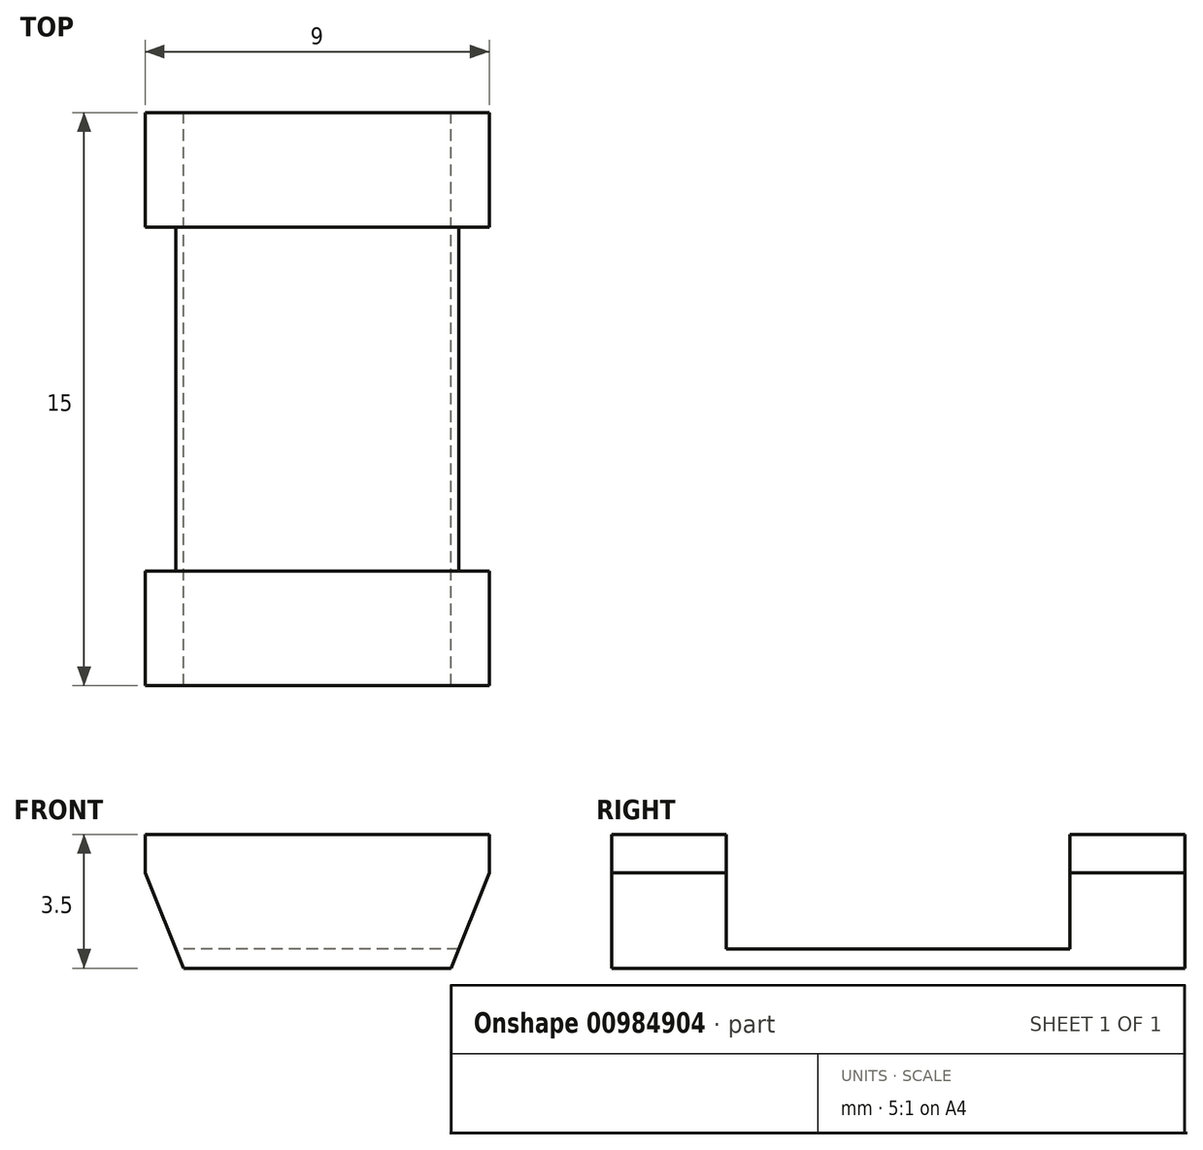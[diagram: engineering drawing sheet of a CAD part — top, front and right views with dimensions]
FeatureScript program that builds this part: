
annotation { "Feature Type Name" : "Feature", "Feature Type Description" : "" }
export const myFeature = defineFeature(function(context is Context, id is Id, definition is map)
    precondition{}
    {
        {
            var Q0;
            Q0=qCreatedBy(makeId("Front.planeOp"),FACE);
            var sketch = newSketch(context, id + "F0", { "sketchPlane" : qUnion([Q0])});
            skLineSegment(sketch, "E0", {"start": v(0, 0) * mm, "end": v(-3.5, 0) * mm});
            skLineSegment(sketch, "E1", {"start": v(3.5, 0) * mm, "end": v(0, 0) * mm});
            skLineSegment(sketch, "E2", {"start": v(-3.5, 0) * mm, "end": v(-4.5, 2.5) * mm});
            skLineSegment(sketch, "E3", {"start": v(-4.5, 2.5) * mm, "end": v(-4.5, 3.5) * mm});
            skLineSegment(sketch, "E4", {"start": v(-4.5, 3.5) * mm, "end": v(0, 3.5) * mm});
            skLineSegment(sketch, "E5", {"start": v(0, 3.5) * mm, "end": v(4.5, 3.5) * mm});
            skLineSegment(sketch, "E6", {"start": v(4.5, 3.5) * mm, "end": v(4.5, 2.5) * mm});
            skLineSegment(sketch, "E7", {"start": v(4.5, 2.5) * mm, "end": v(3.5, 0) * mm});
            skSolve(sketch);
        }
        {
            var Q0;
            Q0 = qSketchRegion(id + "F0", true);
            var Q1;
            Q1=makeQuery(id+"F0.imprint","IMPRINT",FACE,{"disambiguationData":[TD([[makeQuery(id+"F0.imprint","IMPRINT",EDGE,{"derivedFrom":sQuery(id+"F0.wireOp",EDGE,"E0")}),-1.0]])]});
            extrude(context, id + "F1", {"entities" : qUnion([Q0, Q1]), "flatOperationType" : FlatOperationType.REMOVE, "depth" : 15 * mm, "offsetDistance" : 25 * mm, "domain" : OperationDomain.MODEL});
        }
        {
            var Q0;
            Q0=makeQuery(id+"F1.opExtrude","SWEPT_FACE",FACE,{"disambiguationData":[OSD([sQuery(id+"F0.wireOp",EDGE,"E4"),sQuery(id+"F0.wireOp",EDGE,"E5")])]});
            var sketch = newSketch(context, id + "F2", { "sketchPlane" : qUnion([Q0])});
            skLineSegment(sketch, "E8", {"start": v(4.5, -7.5) * mm, "end": v(4.5, -12) * mm});
            skLineSegment(sketch, "E9", {"start": v(4.5, -12) * mm, "end": v(-4.5, -12) * mm});
            skLineSegment(sketch, "E10", {"start": v(-4.5, -12) * mm, "end": v(-4.5, -7.5) * mm});
            skLineSegment(sketch, "E11", {"start": v(-4.5, -7.5) * mm, "end": v(-4.5, -3) * mm});
            skLineSegment(sketch, "E12", {"start": v(-4.5, -3) * mm, "end": v(4.5, -3) * mm});
            skLineSegment(sketch, "E13", {"start": v(4.5, -3) * mm, "end": v(4.5, -7.5) * mm});
            skSolve(sketch);
        }
        {
            var Q0;
            Q0=makeQuery(id+"F2.imprint","IMPRINT",FACE,{"disambiguationData":[TD([[makeQuery(id+"F2.imprint","IMPRINT",EDGE,{"derivedFrom":sQuery(id+"F2.wireOp",EDGE,"E8")}),1.0]])]});
            extrude(context, id + "F3", {"entities" : qUnion([Q0]), "operationType" : NewBodyOperationType.REMOVE, "flatOperationType" : FlatOperationType.REMOVE, "oppositeDirection" : true, "depth" : 3 * mm, "offsetDistance" : 25 * mm, "domain" : OperationDomain.MODEL});
        }
    });
